# Revit family: VT.VAR20.G.07
name_source: partatom
category: Оборудование
units: mm (PartAtom-declared; Revit-internal decimal feet)

## family parameters
Всегда вертикально = Да
Заголовок OmniClass = Climate Control (HVAC)
На основе рабочей плоскости = Нет
Номер OmniClass = 23.75.00.00
Общий = Нет
При загрузке вырезать с полостями = Нет
Размер круглого соединителя = Использовать диаметр
Тип детали = Нормальный
Точка расчета площади = Нет

## types (1)
- VT.VAR20.G.07
    BIMобъект категории = Другие
    BIMобъект основная категория = Водопровод
    IFC Classification = Клапан
    Revit Version = 2018
    SKU продукта = VARIMIX
    URL = https://valtec.ru
    URL бренда = https://valtec.ru
    URL продукта = https://valtec.ru
    Uniclass 1.4 Описание = Климат-контроль установки и оборудование (HVAC)
    Uniclass 2.0 Описание = Клапаны
    Uniclass 2015 Name = Heating, cooling and refrigeration systems
    Uniformat II Описание = HVAC
    Weight Net (Kg) = 0
    Гидравлический возвратный поток = 0.0 л/с
    Гидравлический поток подачи = 0.0 л/с
    Группа модели = VAR 20-21-22-23 с вращающимся приводом
    Группа товаров = VARIMIX
    Изготовитель = IVAR
    Инструкция по установке = https://valtec.ru
    Код категории BIMобъекта = Водопроводным-другой
    Код основной категории BIMobject = Водопровод
    Линия продуктов = ТЕПЛОВАЯ ЭЛЕКТРОСТАНЦИЯ
    Макс рабочая температура (°C) = 120 °C
    Макс рабочее давление (бар) = 10 Па
    Максимальный расход = 3000 l/h
    Мастерформат 2014 Описание = Отопление, вентиляция и кондиционирование воздуха (HVAC)
    Материал = Латунь - CW617N
    Материал основной = Латунь
    Номинальная высота = 0 мм
    Номинальная ширина = 0 мм
    Общий поток подачи гидравлики = 0.0 л/с
    Описание = Низкотемпературный смесительный комплект с 3 или 4-ходовым смесительным клапаном для системы VARIMIX
    Описание NBS = Клапаны
    Описание OmniClass = HVAC Специальные продукты и оборудование
    Описание Конфигурации = Низкотемпературный смесительный комплект, оснащенный 3 или 4-ходовым смесительным клапаном для системы VARIMIX.
    Описание статьи = Низкотемпературный смесительный комплект с 3 или 4-ходовым смесительным клапаном для системы VARIMIX
    Пенополистрирольная теплоизоляция = Да
    Полный гидравлический возвратный поток = 0.0 л/с
    Практическое руководство по использованию семьи = - Вы можете выбрать один и только один коэффициент расхода. Отметьте эту опцию в параметрах «Свойства модели - Kv 2.00» или «Свойства модели - Kv 4.00» или «Свойства модели - Kv 8.00».
- Вы можете выбрать между двумя температурными категориями смесительного клапана. Отметьте эту опцию в параметрах «Свойства модели - смесительный клапан, подходящий для высокотемпературного теплогенератора» или «Свойства модели - смесительный клапан, подходящий для низкотемпературного теплогенератора».
- Вы можете выбрать один и только один тип насоса. Отметьте эту опцию в параметрах «Свойства модели - нет насоса» или «Свойства модели - электронный насос с переменной скоростью» или «Свойства модели - трехскоростной стандартный насос».
- Вы можете выбрать версию с байпасом перепада давления или без него. Отметьте эту опцию в параметрах «Свойства модели - с байпасом перепада давления» или «Свойства модели - без байпаса перепада давления».
- Вы можете выбрать один из двух типов смесительных клапанов. Отметьте эту опцию в параметрах «Свойства модели - с трехходовым смесительным клапаном» или «Свойства модели - с четырехходовым смесительным клапаном».
    Произведено в = Сделано в Италии
    Размер соединения = G 1"1/4 M
    Размеры соединения насоса = G 1"1/2 M
    Семейная версия = Rev.00
    Семейство продуктов = Тепловая электростанция
    Страна изготовитель = Italy
    Техническое описание = https://valtec.ru
    Тип статьи = VAR 20-21-22-23 с вращающимся приводом
